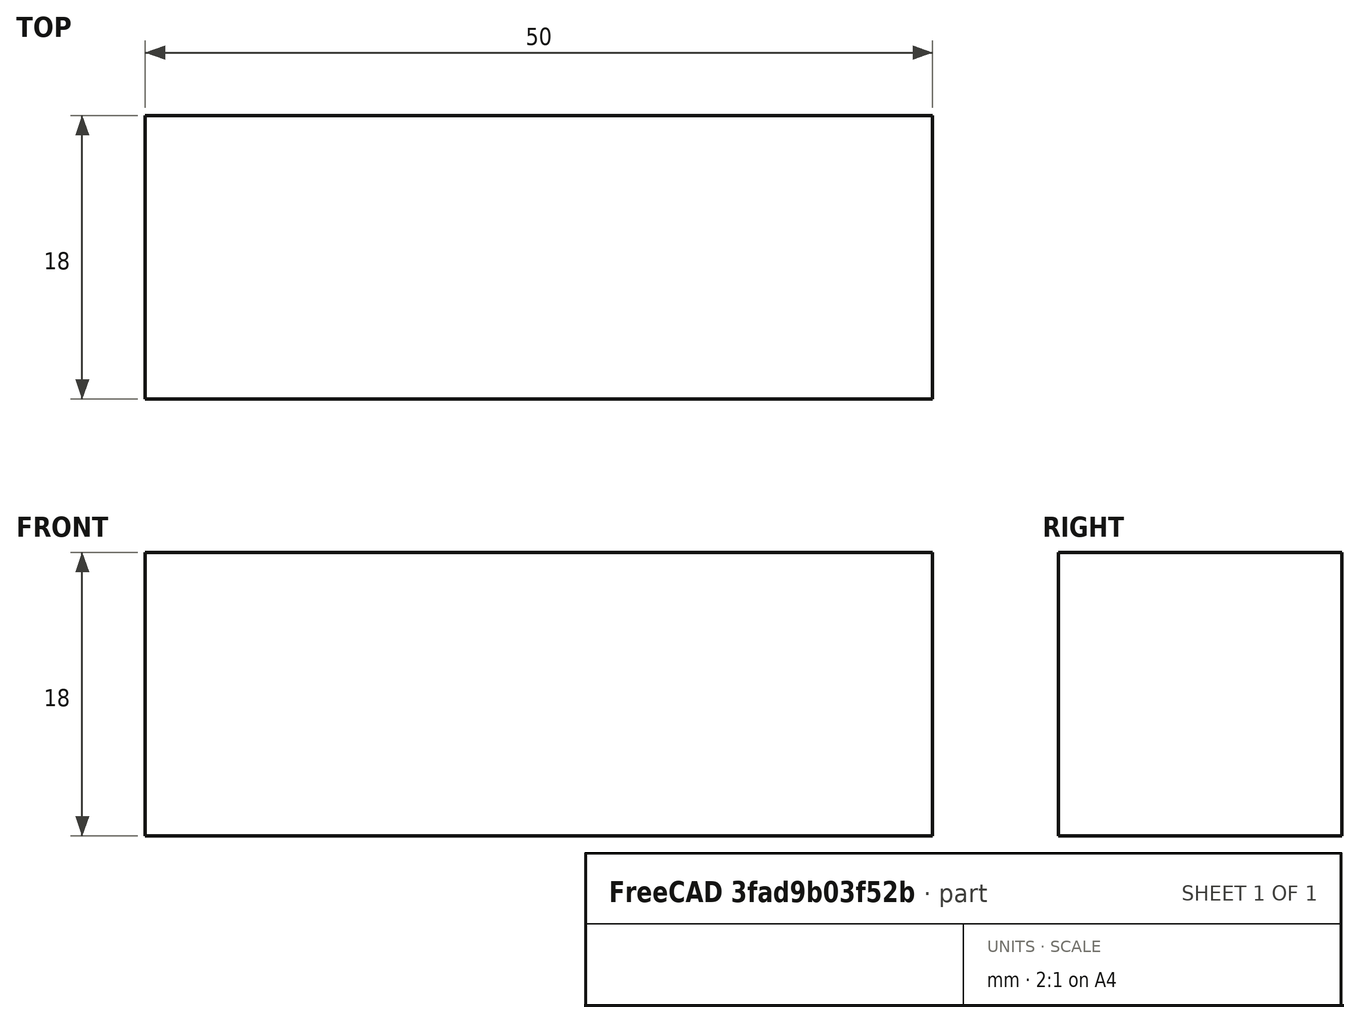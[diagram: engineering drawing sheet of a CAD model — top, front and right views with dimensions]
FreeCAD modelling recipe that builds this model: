
FCSTD DOCUMENT  (FreeCAD 0.19R24276 (Git))
Label: 3000_strut_x_18_18_50
License: All rights reserved
LicenseURL: http://en.wikipedia.org/wiki/All_rights_reserved
objects: Sketcher::SketchObject×1, PartDesign::Pad×1, PartDesign::Body×1
note: 4 computed .brp shape members not serialized (recipe doc carries the construction recipe); baked Part::Feature solids carry a one-line shape summary decoded from their .brp

FEATURE [Sketcher::SketchObject] Sketch
  FullyConstrained = true
  MapMode = 5
  Placement = pos=(0,0,0) rot=(0.57735,0.57735,0.57735;2.0944rad)
  Support = -> [YZ_Plane]
  sketch-geometry (4):
    g0: LineSegment StartX=0 StartY=18 StartZ=0 EndX=18 EndY=18 EndZ=0
    g1: LineSegment StartX=18 StartY=18 StartZ=0 EndX=18 EndY=0 EndZ=0
    g2: LineSegment StartX=18 StartY=0 StartZ=0 EndX=0 EndY=0 EndZ=0
    g3: LineSegment StartX=0 StartY=0 StartZ=0 EndX=0 EndY=18 EndZ=0
  constraints (12):
    c: Coincident(g0,g1)
    c: Coincident(g1,g2)
    c: Coincident(g2,g3)
    c: Coincident(g3,g0)
    c: Horizontal(g0)
    c: Horizontal(g2)
    c: Vertical(g1)
    c: Vertical(g3)
    c: PointOnObject(g0,g-2)
    c: PointOnObject(g1,g-1)
    c: Equal(g1,g0)
    c: DistanceY(g1,g1) = 18
FEATURE [PartDesign::Pad] Pad
  Direction = (1,1,1)
  Length = 50
  Length2 = 100
  Placement = pos=(0,0,0) rot=(0.57735,0.57735,0.57735;2.0944rad)
  Profile = -> Sketch
  Type = 0
  expr: Length = 50
FEATURE [PartDesign::Body] Body
  Group = -> [Sketch,Pad]
  Origin = -> Origin
  Tip = -> Pad
